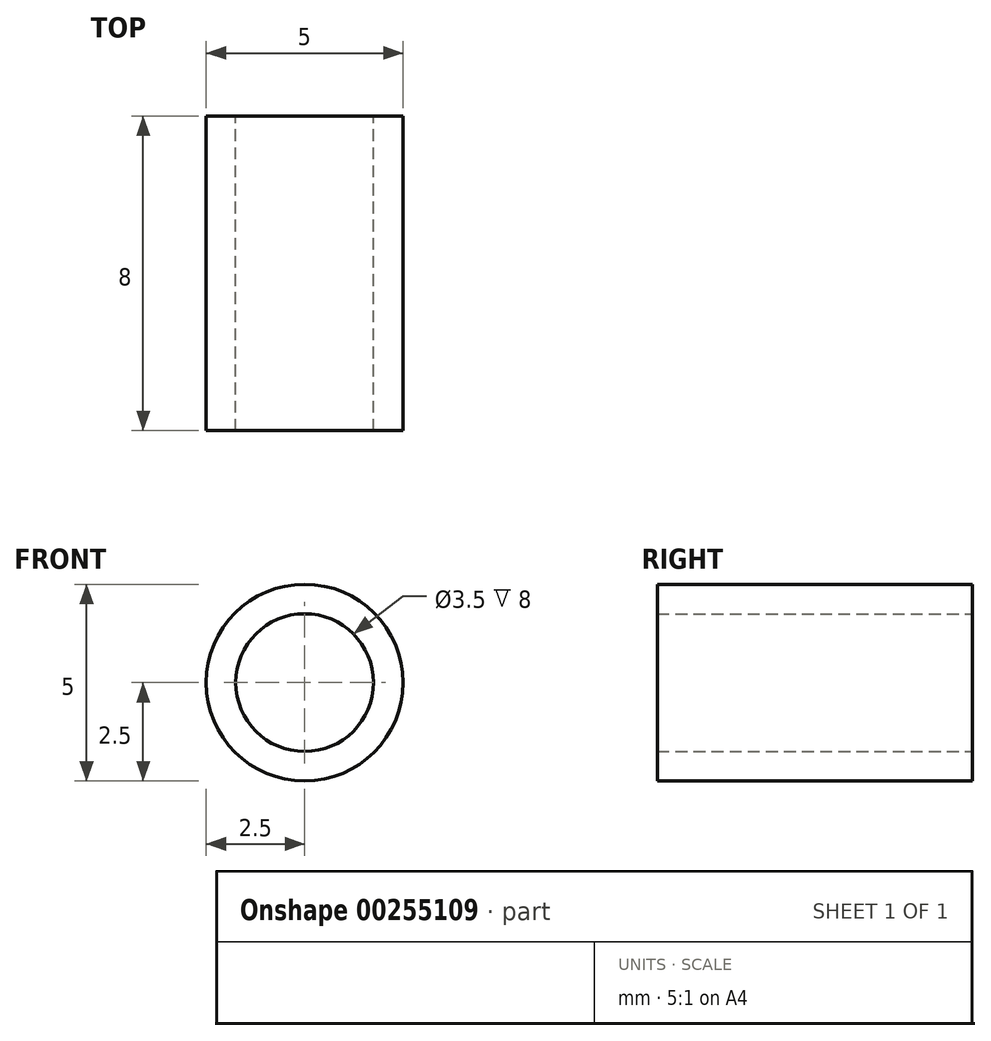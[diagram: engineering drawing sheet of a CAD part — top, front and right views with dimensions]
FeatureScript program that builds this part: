
annotation { "Feature Type Name" : "Feature", "Feature Type Description" : "" }
export const myFeature = defineFeature(function(context is Context, id is Id, definition is map)
    precondition{}
    {
        {
            var Q0;
            Q0=qCreatedBy(makeId("Front.planeOp"),FACE);
            var sketch = newSketch(context, id + "F0", { "sketchPlane" : qUnion([Q0])});
            skCircle(sketch, "E0", {"center": v(0, 0) * mm, "radius": 1.75 * mm});
            skCircle(sketch, "E1", {"center": v(0, 0) * mm, "radius": 2.5 * mm});
            skSolve(sketch);
        }
        {
            var Q0;
            Q0 = qSketchRegion(id + "F0", true);
            extrude(context, id + "F1", {"entities" : qUnion([Q0]), "depth" : 8 * mm});
        }
    });
